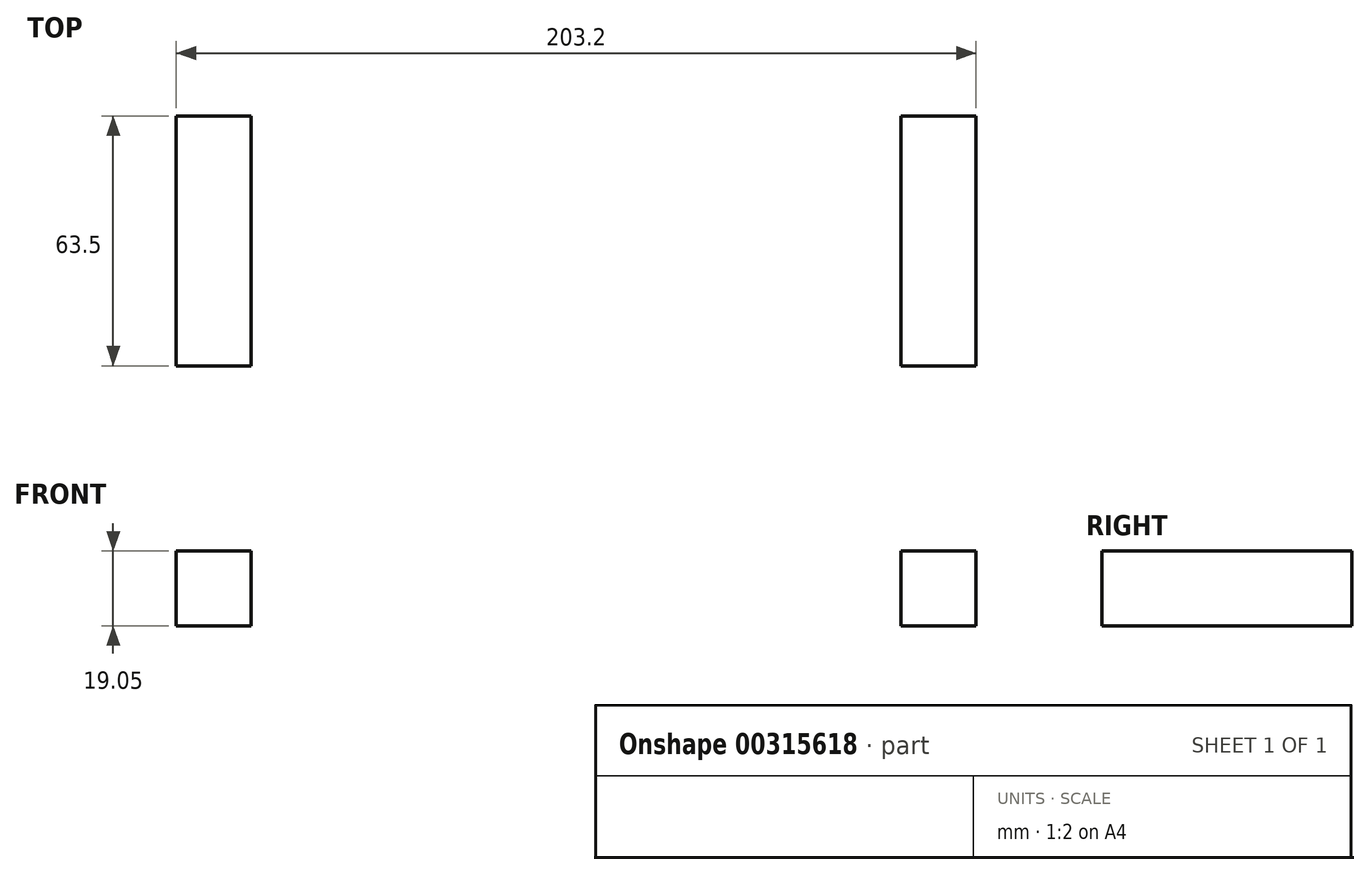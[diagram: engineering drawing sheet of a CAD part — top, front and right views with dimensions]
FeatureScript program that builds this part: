
annotation { "Feature Type Name" : "Feature", "Feature Type Description" : "" }
export const myFeature = defineFeature(function(context is Context, id is Id, definition is map)
    precondition{}
    {
        {
            var Q0;
            Q0=qCreatedBy(makeId("Top.planeOp"),FACE);
            var sketch = newSketch(context, id + "F0", { "sketchPlane" : qUnion([Q0])});
            skLineSegment(sketch, "E0.bottom", {"start": v(-101.6, 139.7) * mm, "end": v(101.6, 139.7) * mm});
            skLineSegment(sketch, "E0.top", {"start": v(-101.6, -139.7) * mm, "end": v(101.6, -139.7) * mm});
            skLineSegment(sketch, "E0.left", {"start": v(-101.6, 139.7) * mm, "end": v(-101.6, -139.7) * mm});
            skLineSegment(sketch, "E0.right", {"start": v(101.6, 139.7) * mm, "end": v(101.6, -139.7) * mm});
            skPoint(sketch, "E0.middle", {"position": v(0, 0) * mm});
            skLineSegment(sketch, "E1.bottom", {"start": v(-63.5, 114.3) * mm, "end": v(63.5, 114.3) * mm});
            skLineSegment(sketch, "E1.top", {"start": v(-63.5, -114.3) * mm, "end": v(63.5, -114.3) * mm});
            skLineSegment(sketch, "E1.left", {"start": v(-63.5, 114.3) * mm, "end": v(-63.5, -114.3) * mm});
            skLineSegment(sketch, "E1.right", {"start": v(63.5, 114.3) * mm, "end": v(63.5, -114.3) * mm});
            skLineSegment(sketch, "E2", {"start": v(-101.6, 76.2) * mm, "end": v(101.6, 76.2) * mm, "construction": true});
            skLineSegment(sketch, "E3", {"start": v(-101.6, -76.2) * mm, "end": v(101.6, -76.2) * mm, "construction": true});
            skLineSegment(sketch, "E4", {"start": v(-101.6, 0) * mm, "end": v(101.6, 0) * mm, "construction": true});
            skLineSegment(sketch, "E5.bottom", {"start": v(-101.6, 76.2) * mm, "end": v(-82.55, 76.2) * mm});
            skLineSegment(sketch, "E5.top", {"start": v(-101.6, 139.7) * mm, "end": v(-82.55, 139.7) * mm});
            skLineSegment(sketch, "E5.left", {"start": v(-101.6, 76.2) * mm, "end": v(-101.6, 139.7) * mm});
            skLineSegment(sketch, "E5.right", {"start": v(-82.55, 76.2) * mm, "end": v(-82.55, 139.7) * mm});
            skLineSegment(sketch, "E6.bottom", {"start": v(101.6, 76.2) * mm, "end": v(82.55, 76.2) * mm});
            skLineSegment(sketch, "E6.top", {"start": v(101.6, 139.7) * mm, "end": v(82.55, 139.7) * mm});
            skLineSegment(sketch, "E6.left", {"start": v(101.6, 76.2) * mm, "end": v(101.6, 139.7) * mm});
            skLineSegment(sketch, "E6.right", {"start": v(82.55, 76.2) * mm, "end": v(82.55, 139.7) * mm});
            skLineSegment(sketch, "E7.bottom", {"start": v(101.6, -76.2) * mm, "end": v(82.55, -76.2) * mm});
            skLineSegment(sketch, "E7.top", {"start": v(101.6, -139.7) * mm, "end": v(82.55, -139.7) * mm});
            skLineSegment(sketch, "E7.left", {"start": v(101.6, -76.2) * mm, "end": v(101.6, -139.7) * mm});
            skLineSegment(sketch, "E7.right", {"start": v(82.55, -76.2) * mm, "end": v(82.55, -139.7) * mm});
            skLineSegment(sketch, "E8.bottom", {"start": v(-101.6, -76.2) * mm, "end": v(-82.55, -76.2) * mm});
            skLineSegment(sketch, "E8.top", {"start": v(-101.6, -139.7) * mm, "end": v(-82.55, -139.7) * mm});
            skLineSegment(sketch, "E8.left", {"start": v(-101.6, -76.2) * mm, "end": v(-101.6, -139.7) * mm});
            skLineSegment(sketch, "E8.right", {"start": v(-82.55, -76.2) * mm, "end": v(-82.55, -139.7) * mm});
            skLineSegment(sketch, "E9.bottom", {"start": v(-120.65, 25.4) * mm, "end": v(-82.55, 25.4) * mm});
            skLineSegment(sketch, "E9.top", {"start": v(-120.65, -25.4) * mm, "end": v(-82.55, -25.4) * mm});
            skLineSegment(sketch, "E9.left", {"start": v(-120.65, 25.4) * mm, "end": v(-120.65, -25.4) * mm});
            skLineSegment(sketch, "E9.right", {"start": v(-82.55, 25.4) * mm, "end": v(-82.55, -25.4) * mm});
            skPoint(sketch, "E9.middle", {"position": v(-101.6, 0) * mm});
            skLineSegment(sketch, "E10.bottom", {"start": v(82.55, 25.4) * mm, "end": v(120.65, 25.4) * mm});
            skLineSegment(sketch, "E10.top", {"start": v(82.55, -25.4) * mm, "end": v(120.65, -25.4) * mm});
            skLineSegment(sketch, "E10.left", {"start": v(82.55, 25.4) * mm, "end": v(82.55, -25.4) * mm});
            skLineSegment(sketch, "E10.right", {"start": v(120.65, 25.4) * mm, "end": v(120.65, -25.4) * mm});
            skPoint(sketch, "E10.middle", {"position": v(101.6, 0) * mm});
            skSolve(sketch);
        }
        {
            var Q0;
            Q0=makeQuery(id+"F0.imprint","IMPRINT",FACE,{"disambiguationData":[TD([[makeQuery(id+"F0.imprint","IMPRINT",EDGE,{"derivedFrom":sQuery(id+"F0.wireOp",EDGE,"E0.bottom")}),-1.0]])]});
            extrude(context, id + "F1", {"entities" : qUnion([Q0]), "depth" : 19.05 * mm});
        }
        {
            var Q0;
            Q0=makeQuery(id+"F1.opExtrude","CAP_FACE",FACE,{"disambiguationData":[OSD([sQuery(id+"F0.wireOp",EDGE,"E0.bottom"),sQuery(id+"F0.wireOp",EDGE,"E0.top"),sQuery(id+"F0.wireOp",EDGE,"E0.left"),sQuery(id+"F0.wireOp",EDGE,"E0.right"),sQuery(id+"F0.wireOp",EDGE,"E1.bottom"),sQuery(id+"F0.wireOp",EDGE,"E1.top"),sQuery(id+"F0.wireOp",EDGE,"E1.left"),sQuery(id+"F0.wireOp",EDGE,"E1.right"),sQuery(id+"F0.wireOp",EDGE,"E5.bottom"),sQuery(id+"F0.wireOp",EDGE,"E5.right"),sQuery(id+"F0.wireOp",EDGE,"E6.bottom"),sQuery(id+"F0.wireOp",EDGE,"E6.right"),sQuery(id+"F0.wireOp",EDGE,"E7.bottom"),sQuery(id+"F0.wireOp",EDGE,"E7.right"),sQuery(id+"F0.wireOp",EDGE,"E8.bottom"),sQuery(id+"F0.wireOp",EDGE,"E8.right"),sQuery(id+"F0.wireOp",EDGE,"E9.bottom"),sQuery(id+"F0.wireOp",EDGE,"E9.top"),sQuery(id+"F0.wireOp",EDGE,"E9.right"),sQuery(id+"F0.wireOp",EDGE,"E10.bottom"),sQuery(id+"F0.wireOp",EDGE,"E10.top"),sQuery(id+"F0.wireOp",EDGE,"E10.left")])],"isStart":false});
            var sketch = newSketch(context, id + "F2", { "sketchPlane" : qUnion([Q0])});
            skLineSegment(sketch, "E11.bottom", {"start": v(-69.85, 120.65) * mm, "end": v(69.85, 120.65) * mm});
            skLineSegment(sketch, "E11.top", {"start": v(-69.85, -120.65) * mm, "end": v(69.85, -120.65) * mm});
            skLineSegment(sketch, "E11.left", {"start": v(-69.85, 120.65) * mm, "end": v(-69.85, -120.65) * mm});
            skLineSegment(sketch, "E11.right", {"start": v(69.85, 120.65) * mm, "end": v(69.85, -120.65) * mm});
            skPoint(sketch, "E11.middle", {"position": v(0, 0) * mm});
            skLineSegment(sketch, "E12.bottom", {"start": v(-73.03, 123.83) * mm, "end": v(73.03, 123.83) * mm});
            skLineSegment(sketch, "E12.top", {"start": v(-73.03, -123.83) * mm, "end": v(73.03, -123.83) * mm});
            skLineSegment(sketch, "E12.left", {"start": v(-73.02, 123.83) * mm, "end": v(-73.02, -123.83) * mm});
            skLineSegment(sketch, "E12.right", {"start": v(73.02, 123.83) * mm, "end": v(73.02, -123.83) * mm});
            skSolve(sketch);
        }
        {
            var Q0;
            Q0 = qSketchRegion(id + "F2", true);
            extrude(context, id + "F3", {"entities" : qUnion([Q0]), "operationType" : NewBodyOperationType.REMOVE, "oppositeDirection" : true, "depth" : 3.17 * mm});
        }
    });
